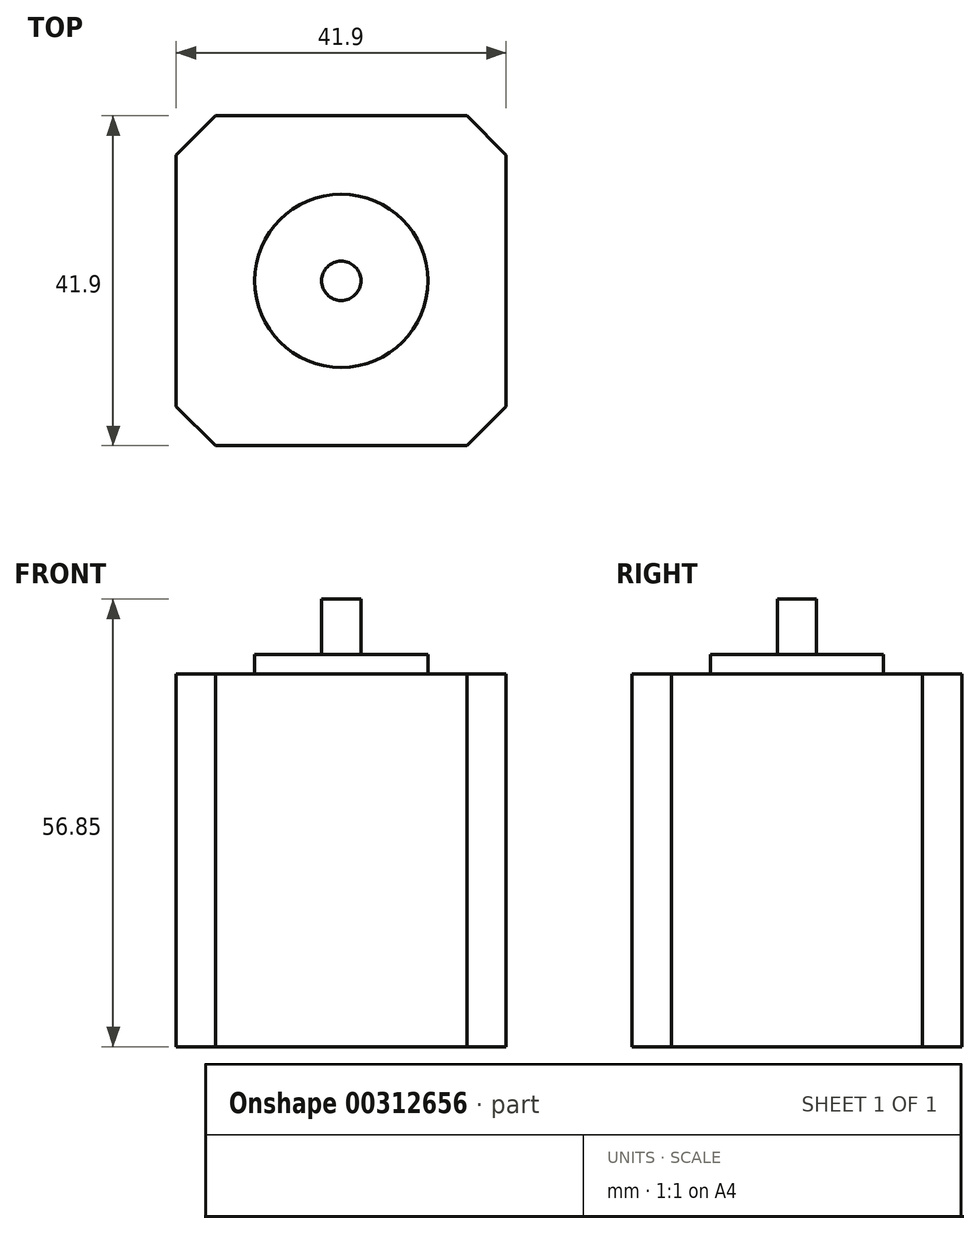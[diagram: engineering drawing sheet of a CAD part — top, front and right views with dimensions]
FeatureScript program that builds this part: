
annotation { "Feature Type Name" : "Feature", "Feature Type Description" : "" }
export const myFeature = defineFeature(function(context is Context, id is Id, definition is map)
    precondition{}
    {
        {
            var Q0;
            Q0=qCreatedBy(makeId("Top.planeOp"),FACE);
            var sketch = newSketch(context, id + "F0", { "sketchPlane" : qUnion([Q0])});
            skLineSegment(sketch, "E0.bottom", {"start": v(-18.1, 25.17) * mm, "end": v(23.8, 25.17) * mm});
            skLineSegment(sketch, "E0.top", {"start": v(-18.1, -16.73) * mm, "end": v(23.8, -16.73) * mm});
            skLineSegment(sketch, "E0.left", {"start": v(-18.1, 25.17) * mm, "end": v(-18.1, -16.73) * mm});
            skLineSegment(sketch, "E0.right", {"start": v(23.8, 25.17) * mm, "end": v(23.8, -16.73) * mm});
            skSolve(sketch);
        }
        {
            var Q0;
            Q0 = qSketchRegion(id + "F0", true);
            extrude(context, id + "F1", {"entities" : qUnion([Q0]), "depth" : 47.35 * mm});
        }
        {
            var Q0;
            Q0=makeQuery(id+"F1.opExtrude","CAP_FACE",FACE,{"disambiguationData":[OSD([sQuery(id+"F0.wireOp",EDGE,"E0.bottom"),sQuery(id+"F0.wireOp",EDGE,"E0.top"),sQuery(id+"F0.wireOp",EDGE,"E0.left"),sQuery(id+"F0.wireOp",EDGE,"E0.right")])],"isStart":false});
            var sketch = newSketch(context, id + "F2", { "sketchPlane" : qUnion([Q0])});
            skPoint(sketch, "E1", {"position": v(2.84, 4.22) * mm});
            skPoint(sketch, "E1.positionSnap0", {"position": v(2.84, 25.17) * mm});
            skPoint(sketch, "E1.positionSnap1", {"position": v(-18.1, 4.22) * mm});
            skCircle(sketch, "E2", {"center": v(2.84, 4.22) * mm, "radius": 11 * mm});
            skSolve(sketch);
        }
        {
            var Q0;
            Q0 = qSketchRegion(id + "F2", true);
            extrude(context, id + "F3", {"entities" : qUnion([Q0]), "operationType" : NewBodyOperationType.ADD, "depth" : 2.5 * mm});
        }
        {
            var Q0;
            Q0=makeQuery(id+"F3.opExtrude","CAP_FACE",FACE,{"disambiguationData":[OSD([sQuery(id+"F2.wireOp",EDGE,"E2")])],"isStart":false});
            var sketch = newSketch(context, id + "F4", { "sketchPlane" : qUnion([Q0])});
            skPoint(sketch, "E3", {"position": v(2.84, 4.22) * mm});
            skCircle(sketch, "E4", {"center": v(2.84, 4.22) * mm, "radius": 2.5 * mm});
            skSolve(sketch);
        }
        {
            var Q0;
            Q0 = qSketchRegion(id + "F4", true);
            extrude(context, id + "F5", {"entities" : qUnion([Q0]), "operationType" : NewBodyOperationType.ADD, "depth" : 7 * mm});
        }
        {
            var Q0;
            Q0=makeQuery(id+"F1.opExtrude","SWEPT_EDGE",EDGE,{"disambiguationData":[OSD([sQuery(id+"F0.wireOp",EDGE,"E0.bottom"),sQuery(id+"F0.wireOp",EDGE,"E0.left")])]});
            var Q1;
            Q1=makeQuery(id+"F1.opExtrude","SWEPT_EDGE",EDGE,{"disambiguationData":[OSD([sQuery(id+"F0.wireOp",EDGE,"E0.top"),sQuery(id+"F0.wireOp",EDGE,"E0.left")])]});
            var Q2;
            Q2=makeQuery(id+"F1.opExtrude","SWEPT_EDGE",EDGE,{"disambiguationData":[OSD([sQuery(id+"F0.wireOp",EDGE,"E0.top"),sQuery(id+"F0.wireOp",EDGE,"E0.right")])]});
            var Q3;
            Q3=makeQuery(id+"F1.opExtrude","SWEPT_EDGE",EDGE,{"disambiguationData":[OSD([sQuery(id+"F0.wireOp",EDGE,"E0.bottom"),sQuery(id+"F0.wireOp",EDGE,"E0.right")])]});
            chamfer(context, id + "F6", {"entities" : qUnion([Q0, Q1, Q2, Q3]), "width" : 5 * mm, "tangentPropagation" : true});
        }
    });
